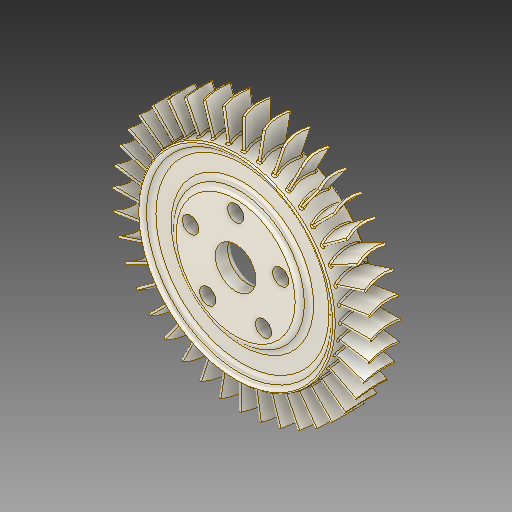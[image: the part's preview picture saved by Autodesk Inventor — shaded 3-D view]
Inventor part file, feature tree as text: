
AUTODESK INVENTOR PART (.ipt)
format: ipt  version: 2019 (Build 230136000, 136)  size: 1,719,296 bytes
history: native  units: mm
features: extrude x6, fillet x6, sketch x5, pattern_circular x2, hole x2
ambient origin geometry x8: Origin, YZ Plane, XZ Plane, XY Plane, X Axis, Y Axis, Z Axis, Center Point
bodies: Solid1 (feature_tree)
feature tree (21):
  sketch  "Sketch1"  dims[d0=145.0mm d1=30.0mm]
  extrude  "Extrusion1"  Depth=30.0mm
  extrude  "Extrusion2"  Depth=30.0mm
  extrude  "Extrusion3"  Depth=40.0mm TaperAngle=0.0deg
  fillet  "Fillet1"  Radius=400.0mm
  pattern_circular  "Circular Pattern1"  Count=30  [1 undecoded]
  extrude  "Extrusion4"  Depth=5.0mm
  extrude  "Extrusion5"  Depth=5.0mm
  fillet  "Fillet2"  Radius=30.0mm
  hole  "Hole1"  [1 undecoded]
  fillet  "Fillet3"  Radius=120.0mm
  fillet  "Fillet4"  Radius=6.0mm
  fillet  "Fillet5"  Radius=2.0mm
  hole  "Hole2"  [1 undecoded]
  pattern_circular  "Circular Pattern2"  [2 undecoded]
  extrude  "Extrusion6"  Depth=5.0mm
  fillet  "Fillet6"  Radius=35.0mm
  sketch  "Sketch2"  dims[d2=30.0mm d3=0.0mm d4=190.0mm]
  sketch  "Sketch3"  dims[d5=10.0mm d6=0.0mm d13=40.0mm d14=0.0mm d15=400.0mm d16=360.0deg]
  sketch  "Sketch4"  dims[d18=1.0mm d19=300.0mm]
  sketch  "Sketch5"  dims[d20=0.0mm d21=0.0mm d23=1.5mm d24=4.0mm d26=30.0mm d28=21.0mm d29=120.0mm d30=6.0mm d31=0.0mm d32=2.0mm d47=10.0mm d48=10.0mm d35=100.0mm d36=6.0mm d37=4.0mm d38=2.0mm d39=90.0deg d40=10.0mm d41=0.0mm d42=2.0mm d44=5.0mm d45=1.0mm d46=35.0mm d49=12.0mm d50=12.0mm d51=6.0mm d52=4.0mm d53=2.0mm d54=90.0deg d55=8.0mm d56=20.594885mm d57=50.0mm d58=360.0deg d67=95.0mm d68=135.0mm d69=5.0mm d70=0.0mm d71=5.0mm]
note: 5 required parameter values undecoded (feature->parameter linkage not recoverable at this tier; creation-order binding heuristic only, values carry confidence <= 0.55)
